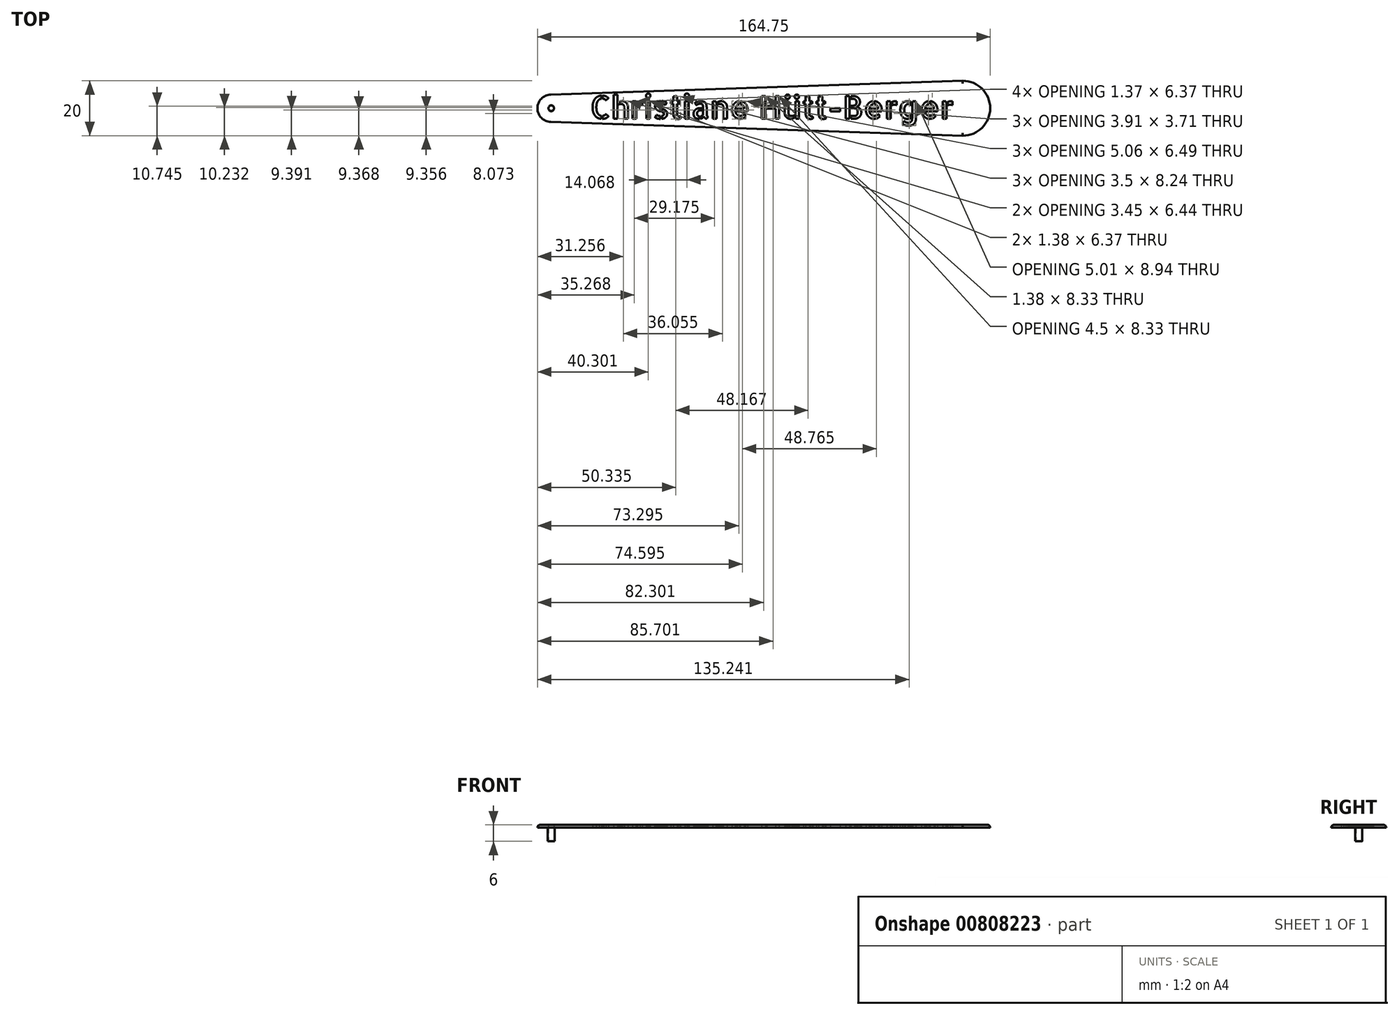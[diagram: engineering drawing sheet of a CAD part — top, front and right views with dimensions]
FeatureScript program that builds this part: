
annotation { "Feature Type Name" : "Feature", "Feature Type Description" : "" }
export const myFeature = defineFeature(function(context is Context, id is Id, definition is map)
    precondition{}
    {
        {
            var Q0;
            Q0=qCreatedBy(makeId("Top.planeOp"),FACE);
            var sketch = newSketch(context, id + "F0", { "sketchPlane" : qUnion([Q0])});
            skCircle(sketch, "E0", {"center": v(0, 0) * mm, "radius": 5 * mm});
            skLineSegment(sketch, "E1", {"start": v(0, 0) * mm, "end": v(149.75, 0) * mm, "construction": true});
            skLineSegment(sketch, "E2", {"start": v(-0.17, -5) * mm, "end": v(149.75, -10) * mm});
            skCircle(sketch, "E3", {"center": v(0, 0) * mm, "radius": 1.25 * mm});
            skLineSegment(sketch, "E4", {"start": v(-0.17, 5) * mm, "end": v(149.75, 10) * mm});
            skLineSegment(sketch, "E5", {"start": v(149.75, 10) * mm, "end": v(149.75, -10) * mm, "construction": true});
            skArc(sketch, "E6", {"start": v(149.08, -9.98) * mm, "mid": v(159.75, 0) * mm, "end": v(149.08, 9.98) * mm});
            skCircle(sketch, "E7", {"center": v(0, 0) * mm, "radius": 1 * mm});
            skSolve(sketch);
        }
        {
            var Q0;
            Q0=makeQuery(id+"F0.imprint","IMPRINT",FACE,{"disambiguationData":[TD([[makeQuery(id+"F0.imprint","IMPRINT",EDGE,{"derivedFrom":sQuery(id+"F0.wireOp",EDGE,"E3")}),-1.0]])]});
            var Q1;
            {var subQ4=sQuery(id+"F0.wireOp",EDGE,"E0");var subQ8=sQuery(id+"F0.wireOp",EDGE,"E2");var subQ17=makeQuery(id+"F0.imprint","INTERSECT",VERTEX,{"derivedFrom":[subQ4,subQ8]});Q1=makeQuery(id+"F0.imprint","IMPRINT",FACE,{"disambiguationData":[TD([[makeQuery(id+"F0.imprint","IMPRINT",EDGE,{"disambiguationData":[TD([[subQ17,-1.0]])],"derivedFrom":subQ4}),-1.0]])]});}
            var Q2;
            {var subQ1=sQuery(id+"F0.wireOp",EDGE,"429c22a2-0887-486a-967f-2b94e1a87693");var subQ8=sQuery(id+"F0.wireOp",EDGE,"E0");var subQ9=makeQuery(id+"F0.imprint","INTERSECT",VERTEX,{"derivedFrom":[subQ8,subQ1]});Q2=makeQuery(id+"F0.imprint","IMPRINT",FACE,{"disambiguationData":[TD([[makeQuery(id+"F0.imprint","IMPRINT",EDGE,{"disambiguationData":[TD([[subQ9,-1.0]])],"derivedFrom":subQ8}),-1.0]])]});}
            var Q3;
            {var subQ0=sQuery(id+"F0.wireOp",EDGE,"9d5f52ef-638e-458b-9d80-165e25f735ae0.MirrorCS");var subQ1=sQuery(id+"F0.wireOp",EDGE,"429c22a2-0887-486a-967f-2b94e1a87693");var subQ2=makeQuery(id+"F0.imprint","INTERSECT",VERTEX,{"disambiguationData":[OD(1.0)],"derivedFrom":[subQ1,subQ0]});Q3=makeQuery(id+"F0.imprint","IMPRINT",FACE,{"disambiguationData":[TD([[makeQuery(id+"F0.imprint","IMPRINT",EDGE,{"disambiguationData":[TD([[subQ2,-1.0]])],"derivedFrom":subQ1}),-1.0]])]});}
            var Q4;
            {var subQ0=sQuery(id+"F0.wireOp",EDGE,"9d5f52ef-638e-458b-9d80-165e25f735ae0.MirrorCS");var subQ1=sQuery(id+"F0.wireOp",EDGE,"429c22a2-0887-486a-967f-2b94e1a87693");var subQ2=makeQuery(id+"F0.imprint","INTERSECT",VERTEX,{"disambiguationData":[OD(2.0)],"derivedFrom":[subQ1,subQ0]});Q4=makeQuery(id+"F0.imprint","IMPRINT",FACE,{"disambiguationData":[TD([[makeQuery(id+"F0.imprint","IMPRINT",EDGE,{"disambiguationData":[TD([[subQ2,-1.0]])],"derivedFrom":subQ1}),1.0]])]});}
            var Q5;
            {var subQ0=sQuery(id+"F0.wireOp",EDGE,"9d5f52ef-638e-458b-9d80-165e25f735ae0.MirrorCS");var subQ1=sQuery(id+"F0.wireOp",EDGE,"429c22a2-0887-486a-967f-2b94e1a87693");var subQ2=makeQuery(id+"F0.imprint","INTERSECT",VERTEX,{"disambiguationData":[OD(0.0)],"derivedFrom":[subQ1,subQ0]});Q5=makeQuery(id+"F0.imprint","IMPRINT",FACE,{"disambiguationData":[TD([[makeQuery(id+"F0.imprint","IMPRINT",EDGE,{"disambiguationData":[TD([[subQ2,1.0]])],"derivedFrom":subQ1}),-1.0]])]});}
            var Q6;
            {var subQ0=sQuery(id+"F0.wireOp",EDGE,"9f0347f5-2bf8-49b9-a686-556642ef9bf0");var subQ1=sQuery(id+"F0.wireOp",EDGE,"9d5f52ef-638e-458b-9d80-165e25f735ae0.MirrorCS");var subQ2=makeQuery(id+"F0.imprint","INTERSECT",VERTEX,{"disambiguationData":[OD(0.0)],"derivedFrom":[subQ1,subQ0]});Q6=makeQuery(id+"F0.imprint","IMPRINT",FACE,{"disambiguationData":[TD([[makeQuery(id+"F0.imprint","IMPRINT",EDGE,{"disambiguationData":[TD([[subQ2,-1.0]])],"derivedFrom":subQ1}),1.0]])]});}
            var Q7;
            {var subQ0=sQuery(id+"F0.wireOp",EDGE,"9f0347f5-2bf8-49b9-a686-556642ef9bf0");var subQ1=sQuery(id+"F0.wireOp",EDGE,"9d5f52ef-638e-458b-9d80-165e25f735ae0.MirrorCS");var subQ2=makeQuery(id+"F0.imprint","INTERSECT",VERTEX,{"disambiguationData":[OD(0.0)],"derivedFrom":[subQ1,subQ0]});Q7=makeQuery(id+"F0.imprint","IMPRINT",FACE,{"disambiguationData":[TD([[makeQuery(id+"F0.imprint","IMPRINT",EDGE,{"disambiguationData":[TD([[subQ2,-1.0]])],"derivedFrom":subQ1}),-1.0]])]});}
            var Q8;
            {var subQ0=sQuery(id+"F0.wireOp",EDGE,"981ca7ae-3106-4b93-b2f6-23ef42e42c5a");var subQ1=sQuery(id+"F0.wireOp",EDGE,"9d5f52ef-638e-458b-9d80-165e25f735ae0.MirrorCS");var subQ3=makeQuery(id+"F0.imprint","INTERSECT",VERTEX,{"derivedFrom":[subQ1,subQ0]});Q8=makeQuery(id+"F0.imprint","IMPRINT",FACE,{"disambiguationData":[TD([[makeQuery(id+"F0.imprint","IMPRINT",EDGE,{"disambiguationData":[TD([[subQ3,1.0]])],"derivedFrom":subQ1}),1.0]])]});}
            var Q9;
            {var subQ0=sQuery(id+"F0.wireOp",EDGE,"981ca7ae-3106-4b93-b2f6-23ef42e42c5a");var subQ2=sQuery(id+"F0.wireOp",EDGE,"E0");var subQ4=makeQuery(id+"F0.imprint","INTERSECT",VERTEX,{"derivedFrom":[subQ2,subQ0]});Q9=makeQuery(id+"F0.imprint","IMPRINT",FACE,{"disambiguationData":[TD([[makeQuery(id+"F0.imprint","IMPRINT",EDGE,{"disambiguationData":[TD([[subQ4,-1.0]])],"derivedFrom":subQ0}),1.0]])]});}
            var Q10;
            {var subQ0=sQuery(id+"F0.wireOp",EDGE,"981ca7ae-3106-4b93-b2f6-23ef42e42c5a");var subQ1=sQuery(id+"F0.wireOp",EDGE,"E0");var subQ3=makeQuery(id+"F0.imprint","INTERSECT",VERTEX,{"derivedFrom":[subQ1,subQ0]});Q10=makeQuery(id+"F0.imprint","IMPRINT",FACE,{"disambiguationData":[TD([[makeQuery(id+"F0.imprint","IMPRINT",EDGE,{"disambiguationData":[TD([[subQ3,-1.0]])],"derivedFrom":subQ1}),1.0]])]});}
            var Q11;
            Q11=makeQuery(id+"F0.imprint","IMPRINT",FACE,{"disambiguationData":[TD([[makeQuery(id+"F0.imprint","IMPRINT",EDGE,{"derivedFrom":sQuery(id+"F0.wireOp",EDGE,"E3")}),1.0]])]});
            extrude(context, id + "F1", {"entities" : qUnion([Q0, Q1, Q2, Q3, Q4, Q5, Q6, Q7, Q8, Q9, Q10, Q11]), "depth" : 1 * mm, "offsetDistance" : 25 * mm});
        }
        {
            var Q0;
            Q0=makeQuery(id+"F0.imprint","IMPRINT",FACE,{"disambiguationData":[TD([[makeQuery(id+"F0.imprint","IMPRINT",EDGE,{"derivedFrom":sQuery(id+"F0.wireOp",EDGE,"E3")}),1.0]])]});
            var Q1;
            Q1=makeQuery(id+"F0.imprint","IMPRINT",FACE,{"disambiguationData":[TD([[makeQuery(id+"F0.imprint","IMPRINT",EDGE,{"derivedFrom":sQuery(id+"F0.wireOp",EDGE,"E3")}),1.0]])]});
            extrude(context, id + "F2", {"entities" : qUnion([Q0, Q1]), "operationType" : NewBodyOperationType.ADD, "oppositeDirection" : true, "depth" : 5 * mm, "offsetDistance" : 25 * mm});
        }
        {
            var Q0;
            Q0=qCreatedBy(makeId("Top.planeOp"),FACE);
            var sketch = newSketch(context, id + "F3", { "sketchPlane" : qUnion([Q0])});
            skText(sketch, "E8", { "text": "Christiane Hütt-Berger", "fontName": "AllertaStencil-Regular.ttf"});
            const initialGuessF3  = {"E8": [0.01415, -0.00383, 1, 0, 0.00833]};
            skSetInitialGuess(sketch, initialGuessF3);
            skSolve(sketch);
        }
        {
            var Q0;
            Q0=qSketchRegion(id+"F3",true);
            extrude(context, id + "F4", {"entities" : qUnion([Q0]), "operationType" : NewBodyOperationType.REMOVE, "depth" : 25 * mm, "offsetDistance" : 25 * mm});
        }
        {
            var Q0;
            Q0=makeQuery(id+"F1.opExtrude","CAP_EDGE",EDGE,{"disambiguationData":[OSD([sQuery(id+"F0.wireOp",EDGE,"E0")])],"isStart":false});
            var Q1;
            Q1=makeQuery(id+"F1.opExtrude","CAP_EDGE",EDGE,{"disambiguationData":[OSD([sQuery(id+"F0.wireOp",EDGE,"E4")])],"isStart":false});
            var Q2;
            Q2=makeQuery(id+"F1.opExtrude","CAP_EDGE",EDGE,{"disambiguationData":[OSD([sQuery(id+"F0.wireOp",EDGE,"E2")])],"isStart":false});
            var Q3;
            Q3=makeQuery(id+"F1.opExtrude","CAP_EDGE",EDGE,{"disambiguationData":[OSD([sQuery(id+"F0.wireOp",EDGE,"E6")])],"isStart":false});
            fillet(context, id + "F5", {"entities" : qUnion([Q0, Q1, Q2, Q3]), "radius" : 1 * mm, "tangentPropagation" : true, "allowEdgeOverflow" : false});
        }
    });
